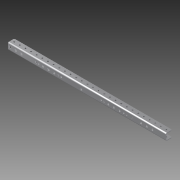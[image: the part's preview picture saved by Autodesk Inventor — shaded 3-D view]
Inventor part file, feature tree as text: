
AUTODESK INVENTOR PART (.ipt)
format: ipt  version: 2014 (Build 180170000, 170)  size: 181,760 bytes
history: native  units: in
note: dims shown in document units (in); Inventor stores cm internally (conversion verified against a paired STEP export)
features: sketch x3, extrude x2, chamfer x1, hole x1, pattern_linear x1
ambient origin geometry x8: Origin, YZ Plane, XZ Plane, XY Plane, X Axis, Y Axis, Z Axis, Center Point
bodies: Solid1 (feature_tree)
feature tree (8):
  extrude  "Extrusion1"  Depth=0.125in TaperAngle=45.0deg
  chamfer  "Chamfer1"  Distance=1.0in
  hole  "Hole1"  [1 undecoded]
  pattern_linear  "Rectangular Pattern1"  [2 undecoded]
  extrude  "Extrusion2"  [1 undecoded]
  sketch  "Sketch1"  dims[d0=28.0in d1=0.0in d2=0.125in d3=0.125in d4=45.0deg]
  sketch  "Sketch2"  dims[d5=0.5in]
  sketch  "Sketch3"  dims[d6=0.5in d7=0.264in d8=0.75in d9=0.375in d10=0.25in d11=0.5635in d12=1.0in d13=0.8108in d14=11.811in d16=1.0in d17=1.0in d18=0.0in]
note: 4 required parameter values undecoded (feature->parameter linkage not recoverable at this tier; creation-order binding heuristic only, values carry confidence <= 0.55)
